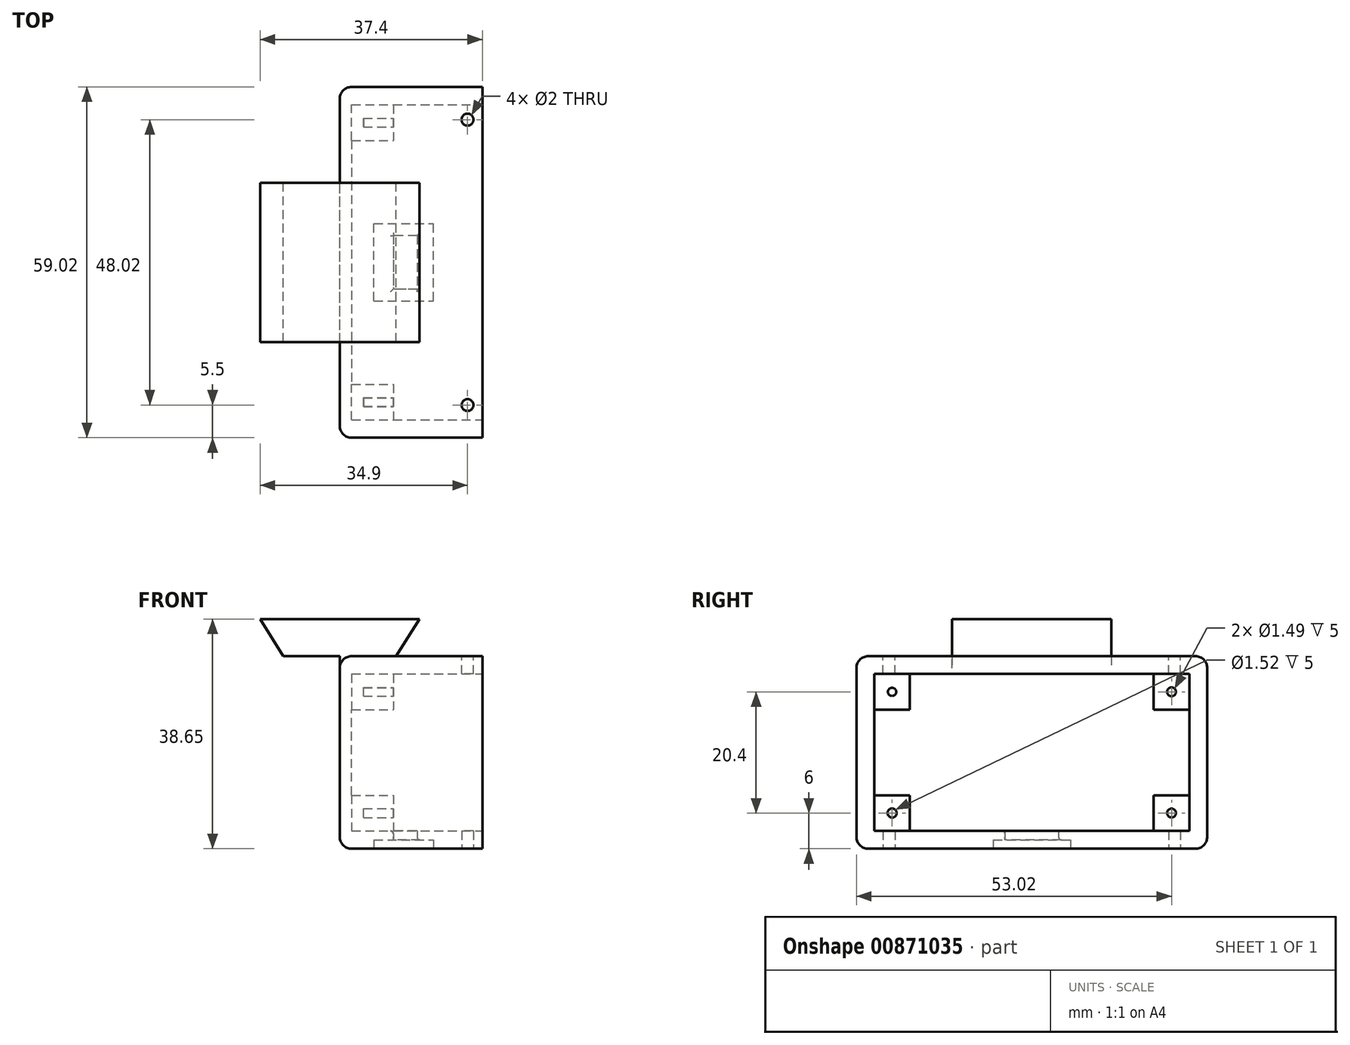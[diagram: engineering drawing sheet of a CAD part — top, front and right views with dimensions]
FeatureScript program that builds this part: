
annotation { "Feature Type Name" : "Feature", "Feature Type Description" : "" }
export const myFeature = defineFeature(function(context is Context, id is Id, definition is map)
    precondition{}
    {
        {
            var Q0;
            Q0=qCreatedBy(makeId("Front.planeOp"),FACE);
            var sketch = newSketch(context, id + "F0", { "sketchPlane" : qUnion([Q0])});
            skLineSegment(sketch, "E0", {"start": v(-13.4, 0) * mm, "end": v(13.4, 0) * mm});
            skLineSegment(sketch, "E1", {"start": v(13.4, 0) * mm, "end": v(9.5, -6.25) * mm});
            skLineSegment(sketch, "E2", {"start": v(9.5, -6.25) * mm, "end": v(-9.5, -6.25) * mm});
            skLineSegment(sketch, "E3", {"start": v(-9.5, -6.25) * mm, "end": v(-13.4, 0) * mm});
            skSolve(sketch);
        }
        {
            var Q0;
            Q0=makeQuery(id+"F0.imprint","IMPRINT",FACE,{"disambiguationData":[TD([[makeQuery(id+"F0.imprint","IMPRINT",EDGE,{"derivedFrom":sQuery(id+"F0.wireOp",EDGE,"E0")}),-1.0]])]});
            extrude(context, id + "F1", {"entities" : qUnion([Q0]), "depth" : 26.8 * mm, "offsetDistance" : 25 * mm});
        }
        {
            var Q0;
            Q0=makeQuery(id+"F1.opExtrude","SWEPT_FACE",FACE,{"disambiguationData":[OSD([sQuery(id+"F0.wireOp",EDGE,"E2")])]});
            var sketch = newSketch(context, id + "F2", { "sketchPlane" : qUnion([Q0])});
            skLineSegment(sketch, "E4.bottom", {"start": v(0, 42.91) * mm, "end": v(24, 42.91) * mm});
            skLineSegment(sketch, "E4.top", {"start": v(0, -16.1) * mm, "end": v(24, -16.1) * mm});
            skLineSegment(sketch, "E4.left", {"start": v(0, 42.91) * mm, "end": v(0, -16.1) * mm});
            skLineSegment(sketch, "E4.right", {"start": v(24, 42.91) * mm, "end": v(24, -16.1) * mm});
            skSolve(sketch);
        }
        {
            var Q0;
            {var subQ1=sQuery(id+"F0.wireOp",EDGE,"E2");var subQ6=makeQuery(id+"F1.opExtrude","SWEPT_EDGE",EDGE,{"disambiguationData":[OSD([sQuery(id+"F0.wireOp",EDGE,"E1"),subQ1])]});Q0=makeQuery(id+"F2.imprint","IMPRINT",FACE,{"disambiguationData":[TD([[makeQuery(id+"F2.imprint","IMPRINT",EDGE,{"derivedFrom":subQ6}),-1.0]])]});}
            var Q1;
            {var subQ5=sQuery(id+"F2.wireOp",EDGE,"E4.bottom");Q1=makeQuery(id+"F2.imprint","IMPRINT",FACE,{"disambiguationData":[TD([[makeQuery(id+"F2.imprint","IMPRINT",EDGE,{"derivedFrom":subQ5}),-1.0]])]});}
            extrude(context, id + "F3", {"entities" : qUnion([Q0, Q1]), "operationType" : NewBodyOperationType.ADD, "depth" : 32.4 * mm, "offsetDistance" : 25 * mm});
        }
        {
            var Q0;
            Q0=makeQuery(id+"F3.opExtrude","SWEPT_FACE",FACE,{"disambiguationData":[OSD([sQuery(id+"F2.wireOp",EDGE,"E4.right")])]});
            var sketch = newSketch(context, id + "F4", { "sketchPlane" : qUnion([Q0])});
            skLineSegment(sketch, "E5.bottom", {"start": v(13.11, -35.65) * mm, "end": v(-39.91, -35.65) * mm});
            skLineSegment(sketch, "E5.top", {"start": v(13.1, -9.25) * mm, "end": v(-39.91, -9.25) * mm});
            skLineSegment(sketch, "E5.left", {"start": v(13.11, -35.65) * mm, "end": v(13.1, -9.25) * mm});
            skLineSegment(sketch, "E5.right", {"start": v(-39.91, -35.65) * mm, "end": v(-39.91, -9.25) * mm});
            skSolve(sketch);
        }
        {
            var Q0;
            Q0=makeQuery(id+"F4.imprint","IMPRINT",FACE,{"disambiguationData":[TD([[makeQuery(id+"F4.imprint","IMPRINT",EDGE,{"derivedFrom":sQuery(id+"F4.wireOp",EDGE,"E5.bottom")}),-1.0]])]});
            extrude(context, id + "F5", {"entities" : qUnion([Q0]), "operationType" : NewBodyOperationType.REMOVE, "oppositeDirection" : true, "depth" : 15 * mm, "offsetDistance" : 25 * mm});
        }
        {
            var Q0;
            Q0=makeQuery(id+"F5.boolean.opBoolean","COPY",FACE,{"derivedFrom":makeQuery(id+"F5.opExtrude","CAP_FACE",FACE,{"disambiguationData":[OSD([sQuery(id+"F4.wireOp",EDGE,"E5.bottom"),sQuery(id+"F4.wireOp",EDGE,"E5.top"),sQuery(id+"F4.wireOp",EDGE,"E5.left"),sQuery(id+"F4.wireOp",EDGE,"E5.right")])],"isStart":false})});
            var sketch = newSketch(context, id + "F6", { "sketchPlane" : qUnion([Q0])});
            skLineSegment(sketch, "E6.bottom", {"start": v(-33.91, -9.25) * mm, "end": v(7.1, -9.25) * mm});
            skLineSegment(sketch, "E6.top", {"start": v(-33.9, -35.65) * mm, "end": v(7.11, -35.65) * mm});
            skLineSegment(sketch, "E6.left", {"start": v(-33.91, -9.25) * mm, "end": v(-33.9, -35.65) * mm});
            skLineSegment(sketch, "E6.right", {"start": v(7.1, -9.25) * mm, "end": v(7.11, -35.65) * mm});
            skSolve(sketch);
        }
        {
            var Q0;
            Q0 = qSketchRegion(id + "F6", true);
            extrude(context, id + "F7", {"entities" : qUnion([Q0]), "operationType" : NewBodyOperationType.REMOVE, "oppositeDirection" : true, "depth" : 7 * mm, "offsetDistance" : 25 * mm});
        }
        {
            var Q0;
            {var subQ0=sQuery(id+"F4.wireOp",EDGE,"E5.right");var subQ1=sQuery(id+"F4.wireOp",EDGE,"E5.top");var subQ2=sQuery(id+"F4.wireOp",EDGE,"E5.bottom");Q0=makeQuery(id+"F7.boolean.opBoolean","SPLIT",FACE,{"disambiguationData":[TD([makeQuery(id+"F5.boolean.opBoolean","COPY",FACE,{"derivedFrom":makeQuery(id+"F5.opExtrude","SWEPT_FACE",FACE,{"disambiguationData":[OSD([subQ0])]})})])],"derivedFrom":makeQuery(id+"F5.boolean.opBoolean","COPY",FACE,{"derivedFrom":makeQuery(id+"F5.opExtrude","CAP_FACE",FACE,{"disambiguationData":[OSD([subQ2,subQ1,sQuery(id+"F4.wireOp",EDGE,"E5.left"),subQ0])],"isStart":false})})});}
            var sketch = newSketch(context, id + "F8", { "sketchPlane" : qUnion([Q0])});
            skLineSegment(sketch, "E7.bottom", {"start": v(-39.91, -15.25) * mm, "end": v(-6.73, -15.25) * mm});
            skLineSegment(sketch, "E7.top", {"start": v(-39.91, -29.65) * mm, "end": v(-6.73, -29.65) * mm});
            skLineSegment(sketch, "E7.left", {"start": v(-39.91, -15.25) * mm, "end": v(-39.91, -29.65) * mm});
            skLineSegment(sketch, "E7.right", {"start": v(-6.73, -15.25) * mm, "end": v(-6.73, -29.65) * mm});
            skSolve(sketch);
        }
        {
            var Q0;
            Q0 = qSketchRegion(id + "F8", true);
            extrude(context, id + "F9", {"entities" : qUnion([Q0]), "operationType" : NewBodyOperationType.REMOVE, "oppositeDirection" : true, "depth" : 7 * mm, "offsetDistance" : 25 * mm});
        }
        {
            var Q0;
            {var subQ0=sQuery(id+"F4.wireOp",EDGE,"E5.left");var subQ1=sQuery(id+"F4.wireOp",EDGE,"E5.top");var subQ2=sQuery(id+"F4.wireOp",EDGE,"E5.bottom");Q0=makeQuery(id+"F7.boolean.opBoolean","SPLIT",FACE,{"disambiguationData":[TD([makeQuery(id+"F5.boolean.opBoolean","COPY",FACE,{"derivedFrom":makeQuery(id+"F5.opExtrude","SWEPT_FACE",FACE,{"disambiguationData":[OSD([subQ0])]})})])],"derivedFrom":makeQuery(id+"F5.boolean.opBoolean","COPY",FACE,{"derivedFrom":makeQuery(id+"F5.opExtrude","CAP_FACE",FACE,{"disambiguationData":[OSD([subQ2,subQ1,subQ0,sQuery(id+"F4.wireOp",EDGE,"E5.right")])],"isStart":false})})});}
            var sketch = newSketch(context, id + "F10", { "sketchPlane" : qUnion([Q0])});
            skLineSegment(sketch, "E8.bottom", {"start": v(-3.04, -15.25) * mm, "end": v(13.1, -15.25) * mm});
            skLineSegment(sketch, "E8.top", {"start": v(-3.04, -29.65) * mm, "end": v(13.1, -29.65) * mm});
            skLineSegment(sketch, "E8.left", {"start": v(-3.04, -15.25) * mm, "end": v(-3.04, -29.65) * mm});
            skLineSegment(sketch, "E8.right", {"start": v(13.1, -15.25) * mm, "end": v(13.11, -29.65) * mm});
            skSolve(sketch);
        }
        {
            var Q0;
            Q0 = qSketchRegion(id + "F10", true);
            extrude(context, id + "F11", {"entities" : qUnion([Q0]), "operationType" : NewBodyOperationType.REMOVE, "oppositeDirection" : true, "depth" : 7 * mm, "offsetDistance" : 25 * mm});
        }
        {
            var Q0;
            {var subQ2=sQuery(id+"F4.wireOp",EDGE,"E5.right");var subQ3=makeQuery(id+"F5.boolean.opBoolean","COPY",FACE,{"derivedFrom":makeQuery(id+"F5.opExtrude","SWEPT_FACE",FACE,{"disambiguationData":[OSD([subQ2])]})});var subQ4=sQuery(id+"F4.wireOp",EDGE,"E5.top");var subQ5=makeQuery(id+"F5.boolean.opBoolean","COPY",FACE,{"derivedFrom":makeQuery(id+"F5.opExtrude","SWEPT_FACE",FACE,{"disambiguationData":[OSD([subQ4])]})});var subQ6=sQuery(id+"F4.wireOp",EDGE,"E5.bottom");Q0=makeQuery(id+"F9.boolean.opBoolean","SPLIT",FACE,{"disambiguationData":[TD([subQ5])],"derivedFrom":makeQuery(id+"F7.boolean.opBoolean","SPLIT",FACE,{"disambiguationData":[TD([subQ3])],"derivedFrom":makeQuery(id+"F5.boolean.opBoolean","COPY",FACE,{"derivedFrom":makeQuery(id+"F5.opExtrude","CAP_FACE",FACE,{"disambiguationData":[OSD([subQ6,subQ4,sQuery(id+"F4.wireOp",EDGE,"E5.left"),subQ2])],"isStart":false})})})});}
            var sketch = newSketch(context, id + "F12", { "sketchPlane" : qUnion([Q0])});
            skCircle(sketch, "E9", {"center": v(-36.91, -12.25) * mm, "radius": 0.7 * mm});
            skSolve(sketch);
        }
        {
            var Q0;
            Q0 = qSketchRegion(id + "F12", true);
            extrude(context, id + "F13", {"entities" : qUnion([Q0]), "operationType" : NewBodyOperationType.REMOVE, "oppositeDirection" : true, "depth" : 5 * mm, "offsetDistance" : 25 * mm});
        }
        {
            var Q0;
            {var subQ1=sQuery(id+"F4.wireOp",EDGE,"E5.top");var subQ2=makeQuery(id+"F5.boolean.opBoolean","COPY",FACE,{"derivedFrom":makeQuery(id+"F5.opExtrude","SWEPT_FACE",FACE,{"disambiguationData":[OSD([subQ1])]})});var subQ4=sQuery(id+"F4.wireOp",EDGE,"E5.left");var subQ5=makeQuery(id+"F5.boolean.opBoolean","COPY",FACE,{"derivedFrom":makeQuery(id+"F5.opExtrude","SWEPT_FACE",FACE,{"disambiguationData":[OSD([subQ4])]})});var subQ6=sQuery(id+"F4.wireOp",EDGE,"E5.bottom");Q0=makeQuery(id+"F11.boolean.opBoolean","SPLIT",FACE,{"disambiguationData":[TD([subQ2])],"derivedFrom":makeQuery(id+"F7.boolean.opBoolean","SPLIT",FACE,{"disambiguationData":[TD([subQ5])],"derivedFrom":makeQuery(id+"F5.boolean.opBoolean","COPY",FACE,{"derivedFrom":makeQuery(id+"F5.opExtrude","CAP_FACE",FACE,{"disambiguationData":[OSD([subQ6,subQ1,subQ4,sQuery(id+"F4.wireOp",EDGE,"E5.right")])],"isStart":false})})})});}
            var sketch = newSketch(context, id + "F14", { "sketchPlane" : qUnion([Q0])});
            skCircle(sketch, "E10", {"center": v(10.1, -12.25) * mm, "radius": 0.75 * mm});
            skSolve(sketch);
        }
        {
            var Q0;
            Q0 = qSketchRegion(id + "F14", true);
            extrude(context, id + "F15", {"entities" : qUnion([Q0]), "operationType" : NewBodyOperationType.REMOVE, "oppositeDirection" : true, "depth" : 5 * mm, "offsetDistance" : 25 * mm});
        }
        {
            var Q0;
            {var subQ2=sQuery(id+"F4.wireOp",EDGE,"E5.right");var subQ3=makeQuery(id+"F5.boolean.opBoolean","COPY",FACE,{"derivedFrom":makeQuery(id+"F5.opExtrude","SWEPT_FACE",FACE,{"disambiguationData":[OSD([subQ2])]})});var subQ4=sQuery(id+"F4.wireOp",EDGE,"E5.bottom");var subQ5=makeQuery(id+"F5.boolean.opBoolean","COPY",FACE,{"derivedFrom":makeQuery(id+"F5.opExtrude","SWEPT_FACE",FACE,{"disambiguationData":[OSD([subQ4])]})});var subQ6=sQuery(id+"F4.wireOp",EDGE,"E5.top");Q0=makeQuery(id+"F9.boolean.opBoolean","SPLIT",FACE,{"disambiguationData":[TD([subQ5])],"derivedFrom":makeQuery(id+"F7.boolean.opBoolean","SPLIT",FACE,{"disambiguationData":[TD([subQ3])],"derivedFrom":makeQuery(id+"F5.boolean.opBoolean","COPY",FACE,{"derivedFrom":makeQuery(id+"F5.opExtrude","CAP_FACE",FACE,{"disambiguationData":[OSD([subQ4,subQ6,sQuery(id+"F4.wireOp",EDGE,"E5.left"),subQ2])],"isStart":false})})})});}
            var sketch = newSketch(context, id + "F16", { "sketchPlane" : qUnion([Q0])});
            skCircle(sketch, "E11", {"center": v(-36.9, -32.65) * mm, "radius": 0.76 * mm});
            skSolve(sketch);
        }
        {
            var Q0;
            Q0 = qSketchRegion(id + "F16", true);
            extrude(context, id + "F17", {"entities" : qUnion([Q0]), "operationType" : NewBodyOperationType.REMOVE, "oppositeDirection" : true, "depth" : 5 * mm, "offsetDistance" : 25 * mm});
        }
        {
            var Q0;
            {var subQ2=sQuery(id+"F4.wireOp",EDGE,"E5.left");var subQ3=makeQuery(id+"F5.boolean.opBoolean","COPY",FACE,{"derivedFrom":makeQuery(id+"F5.opExtrude","SWEPT_FACE",FACE,{"disambiguationData":[OSD([subQ2])]})});var subQ4=sQuery(id+"F4.wireOp",EDGE,"E5.bottom");var subQ5=makeQuery(id+"F5.boolean.opBoolean","COPY",FACE,{"derivedFrom":makeQuery(id+"F5.opExtrude","SWEPT_FACE",FACE,{"disambiguationData":[OSD([subQ4])]})});var subQ6=sQuery(id+"F4.wireOp",EDGE,"E5.top");Q0=makeQuery(id+"F11.boolean.opBoolean","SPLIT",FACE,{"disambiguationData":[TD([subQ5])],"derivedFrom":makeQuery(id+"F7.boolean.opBoolean","SPLIT",FACE,{"disambiguationData":[TD([subQ3])],"derivedFrom":makeQuery(id+"F5.boolean.opBoolean","COPY",FACE,{"derivedFrom":makeQuery(id+"F5.opExtrude","CAP_FACE",FACE,{"disambiguationData":[OSD([subQ4,subQ6,subQ2,sQuery(id+"F4.wireOp",EDGE,"E5.right")])],"isStart":false})})})});}
            var sketch = newSketch(context, id + "F18", { "sketchPlane" : qUnion([Q0])});
            skCircle(sketch, "E12", {"center": v(10.11, -32.65) * mm, "radius": 0.74 * mm});
            skSolve(sketch);
        }
        {
            var Q0;
            Q0 = qSketchRegion(id + "F18", true);
            extrude(context, id + "F19", {"entities" : qUnion([Q0]), "operationType" : NewBodyOperationType.REMOVE, "oppositeDirection" : true, "depth" : 5 * mm, "offsetDistance" : 25 * mm});
        }
        {
            var Q0;
            Q0=makeQuery(id+"F3.opExtrude","CAP_FACE",FACE,{"disambiguationData":[OSD([sQuery(id+"F2.wireOp",EDGE,"E4.bottom"),sQuery(id+"F2.wireOp",EDGE,"E4.top"),sQuery(id+"F2.wireOp",EDGE,"E4.left"),sQuery(id+"F2.wireOp",EDGE,"E4.right")])],"isStart":false});
            var sketch = newSketch(context, id + "F20", { "sketchPlane" : qUnion([Q0])});
            skLineSegment(sketch, "E13.bottom", {"start": v(9, 17.9) * mm, "end": v(13, 17.9) * mm});
            skLineSegment(sketch, "E13.top", {"start": v(9, 8.9) * mm, "end": v(13, 8.9) * mm});
            skLineSegment(sketch, "E13.left", {"start": v(9, 17.9) * mm, "end": v(9, 8.9) * mm});
            skLineSegment(sketch, "E13.right", {"start": v(13, 17.9) * mm, "end": v(13, 8.9) * mm});
            skSolve(sketch);
        }
        {
            var Q0;
            Q0 = qSketchRegion(id + "F20", true);
            extrude(context, id + "F21", {"entities" : qUnion([Q0]), "operationType" : NewBodyOperationType.REMOVE, "oppositeDirection" : true, "depth" : 5 * mm, "offsetDistance" : 25 * mm});
        }
        {
            var Q0;
            Q0=makeQuery(id+"F3.opExtrude","CAP_FACE",FACE,{"disambiguationData":[OSD([sQuery(id+"F2.wireOp",EDGE,"E4.bottom"),sQuery(id+"F2.wireOp",EDGE,"E4.top"),sQuery(id+"F2.wireOp",EDGE,"E4.left"),sQuery(id+"F2.wireOp",EDGE,"E4.right")])],"isStart":false});
            var sketch = newSketch(context, id + "F22", { "sketchPlane" : qUnion([Q0])});
            skLineSegment(sketch, "E14.bottom", {"start": v(5.75, 19.9) * mm, "end": v(15.75, 19.9) * mm});
            skLineSegment(sketch, "E14.top", {"start": v(5.75, 6.9) * mm, "end": v(15.75, 6.9) * mm});
            skLineSegment(sketch, "E14.left", {"start": v(5.75, 19.9) * mm, "end": v(5.75, 6.9) * mm});
            skLineSegment(sketch, "E14.right", {"start": v(15.75, 19.9) * mm, "end": v(15.75, 6.9) * mm});
            skSolve(sketch);
        }
        {
            var Q0;
            Q0 = qSketchRegion(id + "F22", true);
            extrude(context, id + "F23", {"entities" : qUnion([Q0]), "operationType" : NewBodyOperationType.REMOVE, "oppositeDirection" : true, "depth" : 1.5 * mm, "offsetDistance" : 25 * mm});
        }
        {
            var Q0;
            Q0=makeQuery(id+"F23.boolean.opBoolean","COPY",EDGE,{"derivedFrom":makeQuery(id+"F23.opExtrude","CAP_EDGE",EDGE,{"disambiguationData":[OSD([sQuery(id+"F22.wireOp",EDGE,"E14.left")])],"isStart":true})});
            var Q1;
            Q1=makeQuery(id+"F21.boolean.opBoolean","INTERSECT",EDGE,{"derivedFrom":[makeQuery(id+"F7.boolean.opBoolean","MERGE",FACE,{"derivedFrom":[makeQuery(id+"F5.boolean.opBoolean","COPY",FACE,{"derivedFrom":makeQuery(id+"F5.opExtrude","SWEPT_FACE",FACE,{"disambiguationData":[OSD([sQuery(id+"F4.wireOp",EDGE,"E5.bottom")])]})}),makeQuery(id+"F7.opExtrude","SWEPT_FACE",FACE,{"disambiguationData":[OSD([sQuery(id+"F6.wireOp",EDGE,"E6.top")])]})]}),makeQuery(id+"F21.opExtrude","SWEPT_FACE",FACE,{"disambiguationData":[OSD([sQuery(id+"F20.wireOp",EDGE,"E13.left")])]})]});
            var Q2;
            Q2=makeQuery(id+"F23.boolean.opBoolean","INTERSECT",EDGE,{"derivedFrom":[makeQuery(id+"F21.boolean.opBoolean","COPY",FACE,{"derivedFrom":makeQuery(id+"F21.opExtrude","SWEPT_FACE",FACE,{"disambiguationData":[OSD([sQuery(id+"F20.wireOp",EDGE,"E13.right")])]})}),makeQuery(id+"F23.opExtrude","CAP_FACE",FACE,{"disambiguationData":[OSD([sQuery(id+"F22.wireOp",EDGE,"E14.bottom"),sQuery(id+"F22.wireOp",EDGE,"E14.top"),sQuery(id+"F22.wireOp",EDGE,"E14.left"),sQuery(id+"F22.wireOp",EDGE,"E14.right")])],"isStart":false})]});
            var Q3;
            Q3=makeQuery(id+"F23.boolean.opBoolean","COPY",EDGE,{"derivedFrom":makeQuery(id+"F23.opExtrude","CAP_EDGE",EDGE,{"disambiguationData":[OSD([sQuery(id+"F22.wireOp",EDGE,"E14.top")])],"isStart":true})});
            var Q4;
            Q4=makeQuery(id+"F23.boolean.opBoolean","INTERSECT",EDGE,{"derivedFrom":[makeQuery(id+"F21.boolean.opBoolean","COPY",FACE,{"derivedFrom":makeQuery(id+"F21.opExtrude","SWEPT_FACE",FACE,{"disambiguationData":[OSD([sQuery(id+"F20.wireOp",EDGE,"E13.top")])]})}),makeQuery(id+"F23.opExtrude","CAP_FACE",FACE,{"disambiguationData":[OSD([sQuery(id+"F22.wireOp",EDGE,"E14.bottom"),sQuery(id+"F22.wireOp",EDGE,"E14.top"),sQuery(id+"F22.wireOp",EDGE,"E14.left"),sQuery(id+"F22.wireOp",EDGE,"E14.right")])],"isStart":false})]});
            var Q5;
            Q5=makeQuery(id+"F21.boolean.opBoolean","INTERSECT",EDGE,{"derivedFrom":[makeQuery(id+"F7.boolean.opBoolean","MERGE",FACE,{"derivedFrom":[makeQuery(id+"F5.boolean.opBoolean","COPY",FACE,{"derivedFrom":makeQuery(id+"F5.opExtrude","SWEPT_FACE",FACE,{"disambiguationData":[OSD([sQuery(id+"F4.wireOp",EDGE,"E5.bottom")])]})}),makeQuery(id+"F7.opExtrude","SWEPT_FACE",FACE,{"disambiguationData":[OSD([sQuery(id+"F6.wireOp",EDGE,"E6.top")])]})]}),makeQuery(id+"F21.opExtrude","SWEPT_FACE",FACE,{"disambiguationData":[OSD([sQuery(id+"F20.wireOp",EDGE,"E13.bottom")])]})]});
            var Q6;
            Q6=makeQuery(id+"F23.boolean.opBoolean","COPY",EDGE,{"derivedFrom":makeQuery(id+"F23.opExtrude","CAP_EDGE",EDGE,{"disambiguationData":[OSD([sQuery(id+"F22.wireOp",EDGE,"E14.right")])],"isStart":true})});
            var Q7;
            Q7=makeQuery(id+"F23.boolean.opBoolean","COPY",EDGE,{"derivedFrom":makeQuery(id+"F23.opExtrude","CAP_EDGE",EDGE,{"disambiguationData":[OSD([sQuery(id+"F22.wireOp",EDGE,"E14.bottom")])],"isStart":true})});
            fillet(context, id + "F24", {"entities" : qUnion([Q0, Q1, Q2, Q3, Q4, Q5, Q6, Q7]), "radius" : 0.5 * mm, "tangentPropagation" : true, "allowEdgeOverflow" : false});
        }
        {
            var Q0;
            Q0=makeQuery(id+"F3.opExtrude","SWEPT_EDGE",EDGE,{"disambiguationData":[OSD([sQuery(id+"F2.wireOp",EDGE,"E4.bottom"),sQuery(id+"F2.wireOp",EDGE,"E4.left")])]});
            var Q1;
            Q1=makeQuery(id+"F3.opExtrude","CAP_EDGE",EDGE,{"disambiguationData":[OSD([sQuery(id+"F2.wireOp",EDGE,"E4.left")])],"isStart":false});
            var Q2;
            Q2=makeQuery(id+"F3.opExtrude","SWEPT_EDGE",EDGE,{"disambiguationData":[OSD([sQuery(id+"F2.wireOp",EDGE,"E4.top"),sQuery(id+"F2.wireOp",EDGE,"E4.left")])]});
            var Q3;
            Q3=makeQuery(id+"F3.opExtrude","CAP_EDGE",EDGE,{"disambiguationData":[OSD([sQuery(id+"F2.wireOp",EDGE,"E4.bottom")])],"isStart":false});
            var Q4;
            Q4=makeQuery(id+"F3.opExtrude","CAP_EDGE",EDGE,{"disambiguationData":[OSD([sQuery(id+"F2.wireOp",EDGE,"E4.bottom")])],"isStart":true});
            var Q5;
            Q5=makeQuery(id+"F3.opExtrude","CAP_EDGE",EDGE,{"disambiguationData":[OSD([sQuery(id+"F2.wireOp",EDGE,"E4.top")])],"isStart":false});
            var Q6;
            Q6=makeQuery(id+"F3.opExtrude","CAP_EDGE",EDGE,{"disambiguationData":[OSD([sQuery(id+"F2.wireOp",EDGE,"E4.top")])],"isStart":true});
            var Q7;
            {var subQ0=sQuery(id+"F2.wireOp",EDGE,"E4.left");var subQ1=sQuery(id+"F2.wireOp",EDGE,"E4.top");var subQ2=makeQuery(id+"F3.opExtrude","CAP_FACE",FACE,{"disambiguationData":[OSD([sQuery(id+"F2.wireOp",EDGE,"E4.bottom"),subQ1,subQ0,sQuery(id+"F2.wireOp",EDGE,"E4.right")])],"isStart":true});var subQ4=makeQuery(id+"F3.opExtrude","SWEPT_FACE",FACE,{"disambiguationData":[OSD([subQ0])]});Q7=makeQuery(id+"F3.boolean.opBoolean","SPLIT",EDGE,{"disambiguationData":[topologyDisambiguationEdgeConnected([subQ2,subQ4]),TD([makeQuery(id+"F3.opExtrude","SWEPT_FACE",FACE,{"disambiguationData":[OSD([subQ1])]})])],"derivedFrom":makeQuery(id+"F3.opExtrude","CAP_EDGE",EDGE,{"disambiguationData":[OSD([subQ0])],"isStart":true})});}
            var Q8;
            {var subQ0=sQuery(id+"F2.wireOp",EDGE,"E4.bottom");var subQ1=sQuery(id+"F2.wireOp",EDGE,"E4.left");var subQ2=makeQuery(id+"F3.opExtrude","CAP_FACE",FACE,{"disambiguationData":[OSD([subQ0,sQuery(id+"F2.wireOp",EDGE,"E4.top"),subQ1,sQuery(id+"F2.wireOp",EDGE,"E4.right")])],"isStart":true});var subQ4=makeQuery(id+"F3.opExtrude","SWEPT_FACE",FACE,{"disambiguationData":[OSD([subQ1])]});Q8=makeQuery(id+"F3.boolean.opBoolean","SPLIT",EDGE,{"disambiguationData":[topologyDisambiguationEdgeConnected([subQ2,subQ4]),TD([makeQuery(id+"F3.opExtrude","SWEPT_FACE",FACE,{"disambiguationData":[OSD([subQ0])]})])],"derivedFrom":makeQuery(id+"F3.opExtrude","CAP_EDGE",EDGE,{"disambiguationData":[OSD([subQ1])],"isStart":true})});}
            fillet(context, id + "F25", {"entities" : qUnion([Q0, Q1, Q2, Q3, Q4, Q5, Q6, Q7, Q8]), "radius" : 2 * mm, "tangentPropagation" : true, "allowEdgeOverflow" : false});
        }
        {
            var Q0;
            Q0=makeQuery(id+"F3.opExtrude","CAP_FACE",FACE,{"disambiguationData":[OSD([sQuery(id+"F2.wireOp",EDGE,"E4.bottom"),sQuery(id+"F2.wireOp",EDGE,"E4.top"),sQuery(id+"F2.wireOp",EDGE,"E4.left"),sQuery(id+"F2.wireOp",EDGE,"E4.right")])],"isStart":false});
            var sketch = newSketch(context, id + "F26", { "sketchPlane" : qUnion([Q0])});
            skCircle(sketch, "E15", {"center": v(21.5, 37.41) * mm, "radius": 1 * mm});
            skSolve(sketch);
        }
        {
            var Q0;
            Q0 = qSketchRegion(id + "F26", true);
            extrude(context, id + "F27", {"entities" : qUnion([Q0]), "operationType" : NewBodyOperationType.REMOVE, "oppositeDirection" : true, "depth" : 5 * mm, "offsetDistance" : 25 * mm});
        }
        {
            var Q0;
            Q0=makeQuery(id+"F3.opExtrude","CAP_FACE",FACE,{"disambiguationData":[OSD([sQuery(id+"F2.wireOp",EDGE,"E4.bottom"),sQuery(id+"F2.wireOp",EDGE,"E4.top"),sQuery(id+"F2.wireOp",EDGE,"E4.left"),sQuery(id+"F2.wireOp",EDGE,"E4.right")])],"isStart":false});
            var sketch = newSketch(context, id + "F28", { "sketchPlane" : qUnion([Q0])});
            skCircle(sketch, "E16", {"center": v(21.5, -10.6) * mm, "radius": 1 * mm});
            skSolve(sketch);
        }
        {
            var Q0;
            Q0 = qSketchRegion(id + "F28", true);
            extrude(context, id + "F29", {"entities" : qUnion([Q0]), "operationType" : NewBodyOperationType.REMOVE, "oppositeDirection" : true, "depth" : 5 * mm, "offsetDistance" : 25 * mm});
        }
        {
            var Q0;
            Q0=makeQuery(id+"F3.opExtrude","CAP_FACE",FACE,{"disambiguationData":[OSD([sQuery(id+"F2.wireOp",EDGE,"E4.bottom"),sQuery(id+"F2.wireOp",EDGE,"E4.top"),sQuery(id+"F2.wireOp",EDGE,"E4.left"),sQuery(id+"F2.wireOp",EDGE,"E4.right")])],"isStart":true});
            var sketch = newSketch(context, id + "F30", { "sketchPlane" : qUnion([Q0])});
            skCircle(sketch, "E17", {"center": v(21.5, 10.6) * mm, "radius": 1 * mm});
            skSolve(sketch);
        }
        {
            var Q0;
            Q0 = qSketchRegion(id + "F30", true);
            extrude(context, id + "F31", {"entities" : qUnion([Q0]), "operationType" : NewBodyOperationType.REMOVE, "oppositeDirection" : true, "depth" : 5 * mm, "offsetDistance" : 25 * mm});
        }
        {
            var Q0;
            Q0=makeQuery(id+"F3.opExtrude","CAP_FACE",FACE,{"disambiguationData":[OSD([sQuery(id+"F2.wireOp",EDGE,"E4.bottom"),sQuery(id+"F2.wireOp",EDGE,"E4.top"),sQuery(id+"F2.wireOp",EDGE,"E4.left"),sQuery(id+"F2.wireOp",EDGE,"E4.right")])],"isStart":true});
            var sketch = newSketch(context, id + "F32", { "sketchPlane" : qUnion([Q0])});
            skCircle(sketch, "E18", {"center": v(21.5, -37.41) * mm, "radius": 1 * mm});
            skSolve(sketch);
        }
        {
            var Q0;
            Q0 = qSketchRegion(id + "F32", true);
            extrude(context, id + "F33", {"entities" : qUnion([Q0]), "operationType" : NewBodyOperationType.REMOVE, "oppositeDirection" : true, "depth" : 5 * mm, "offsetDistance" : 25 * mm});
        }
    });
